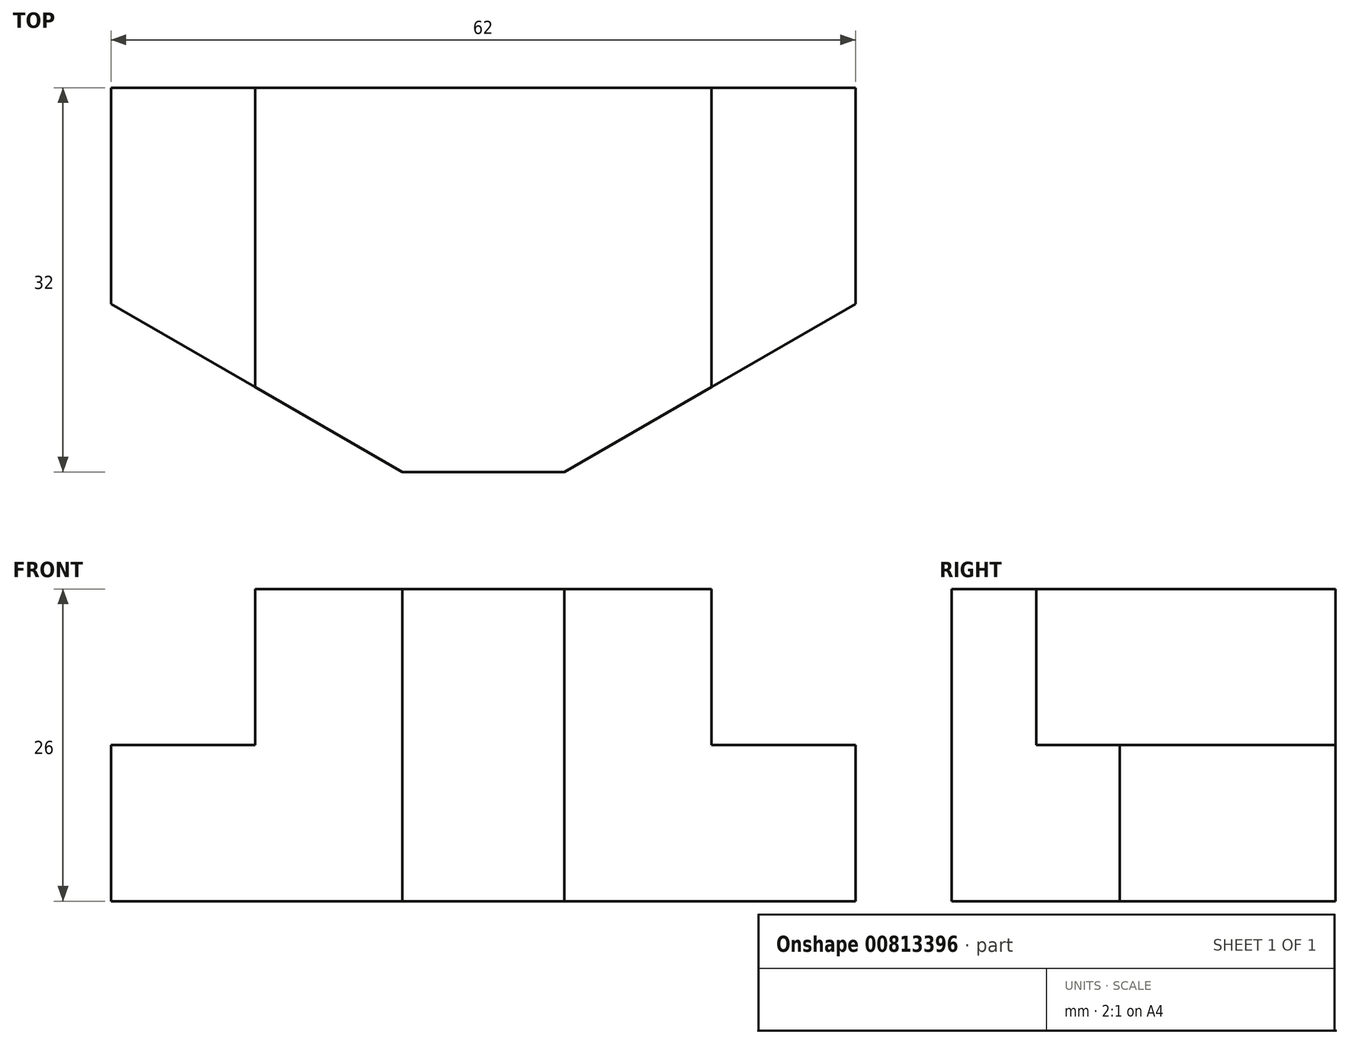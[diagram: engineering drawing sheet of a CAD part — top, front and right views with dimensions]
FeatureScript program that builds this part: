
annotation { "Feature Type Name" : "Feature", "Feature Type Description" : "" }
export const myFeature = defineFeature(function(context is Context, id is Id, definition is map)
    precondition{}
    {
        {
            var Q0;
            Q0=qCreatedBy(makeId("Top.planeOp"),FACE);
            var sketch = newSketch(context, id + "F0", { "sketchPlane" : qUnion([Q0])});
            skLineSegment(sketch, "E0.bottom", {"start": v(0, 0) * mm, "end": v(62, 0) * mm});
            skLineSegment(sketch, "E0.top", {"start": v(0, 32) * mm, "end": v(62, 32) * mm});
            skLineSegment(sketch, "E0.left", {"start": v(0, 0) * mm, "end": v(0, 32) * mm});
            skLineSegment(sketch, "E0.right", {"start": v(62, 0) * mm, "end": v(62, 32) * mm});
            skLineSegment(sketch, "E1", {"start": v(0, 14) * mm, "end": v(24.25, 0) * mm});
            skLineSegment(sketch, "E2", {"start": v(31, 0) * mm, "end": v(31, 9.7) * mm, "construction": true});
            skLineSegment(sketch, "E3.MirrorCS", {"start": v(62, 14) * mm, "end": v(37.75, 0) * mm});
            skLineSegment(sketch, "E4", {"start": v(12, 7.07) * mm, "end": v(12, 32) * mm});
            skLineSegment(sketch, "E5.MirrorCS", {"start": v(50, 7.07) * mm, "end": v(50, 32) * mm});
            skSolve(sketch);
        }
        {
            var Q0;
            {var subQ3=sQuery(id+"F0.wireOp",EDGE,"E4");Q0=makeQuery(id+"F0.imprint","IMPRINT",FACE,{"disambiguationData":[TD([[makeQuery(id+"F0.imprint","IMPRINT",EDGE,{"derivedFrom":subQ3}),1.0]])]});}
            var Q1;
            {var subQ3=sQuery(id+"F0.wireOp",EDGE,"E5.MirrorCS");Q1=makeQuery(id+"F0.imprint","IMPRINT",FACE,{"disambiguationData":[TD([[makeQuery(id+"F0.imprint","IMPRINT",EDGE,{"derivedFrom":subQ3}),-1.0]])]});}
            var Q2;
            {var subQ4=sQuery(id+"F0.wireOp",EDGE,"E4");Q2=makeQuery(id+"F0.imprint","IMPRINT",FACE,{"disambiguationData":[TD([[makeQuery(id+"F0.imprint","IMPRINT",EDGE,{"derivedFrom":subQ4}),-1.0]])]});}
            extrude(context, id + "F1", {"entities" : qUnion([Q0, Q1, Q2]), "depth" : 13 * mm, "offsetDistance" : 25 * mm});
        }
        {
            var Q0;
            {var subQ4=sQuery(id+"F0.wireOp",EDGE,"E4");Q0=makeQuery(id+"F0.imprint","IMPRINT",FACE,{"disambiguationData":[TD([[makeQuery(id+"F0.imprint","IMPRINT",EDGE,{"derivedFrom":subQ4}),-1.0]])]});}
            extrude(context, id + "F2", {"entities" : qUnion([Q0]), "operationType" : NewBodyOperationType.ADD, "depth" : 26 * mm, "offsetDistance" : 25 * mm});
        }
    });
